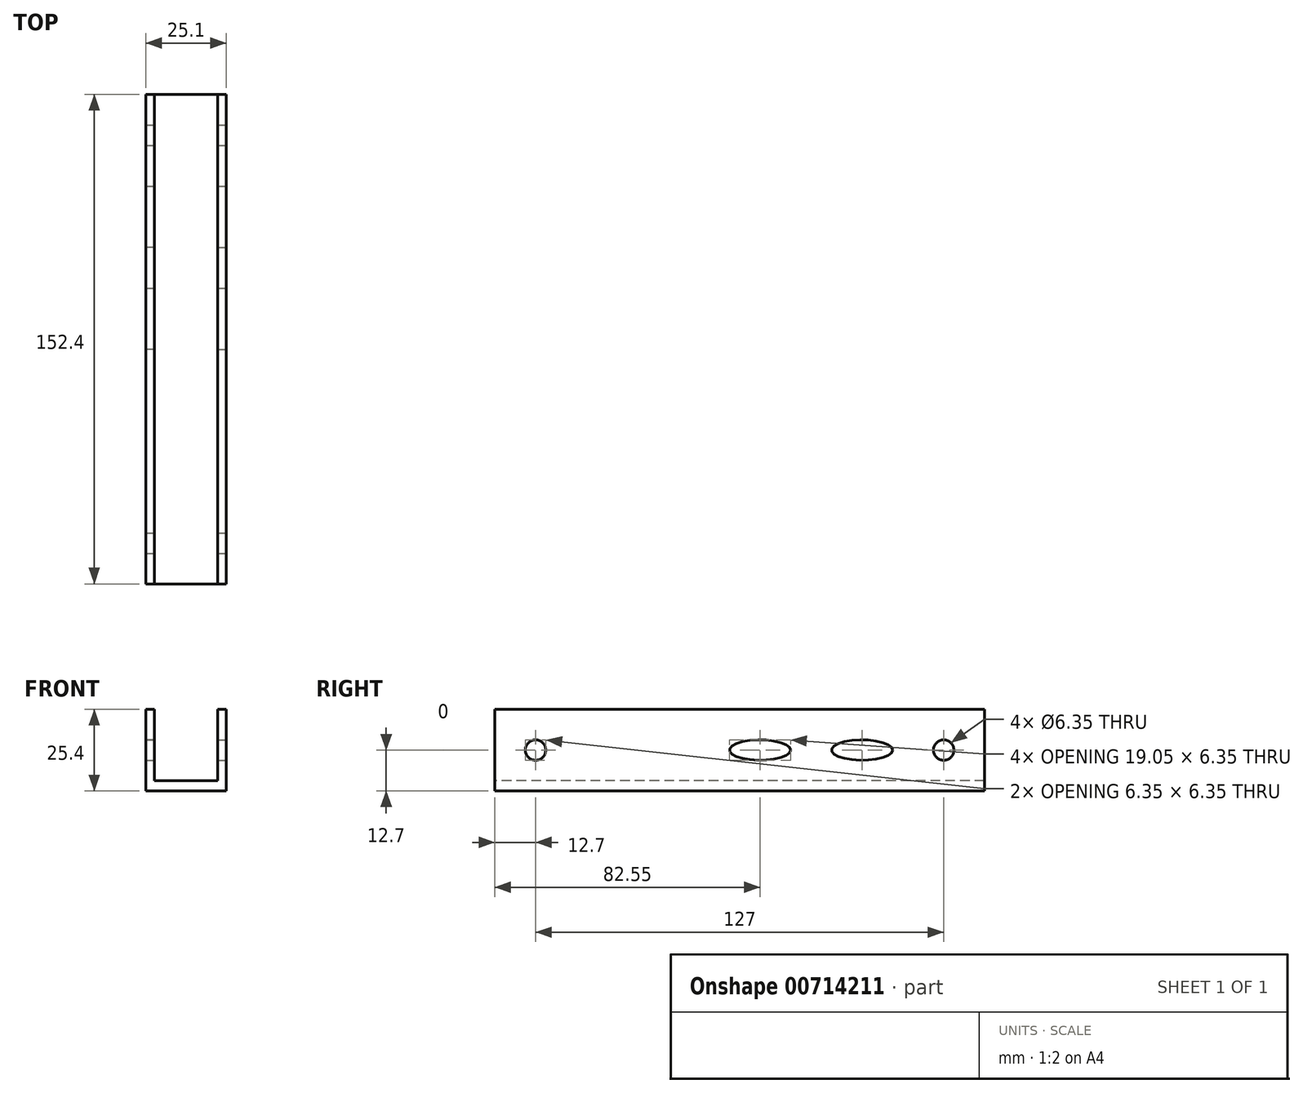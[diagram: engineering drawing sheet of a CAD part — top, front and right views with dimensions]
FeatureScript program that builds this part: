
annotation { "Feature Type Name" : "Feature", "Feature Type Description" : "" }
export const myFeature = defineFeature(function(context is Context, id is Id, definition is map)
    precondition{}
    {
        {
            var Q0;
            Q0=qCreatedBy(makeId("Front.planeOp"),FACE);
            var sketch = newSketch(context, id + "F0", { "sketchPlane" : qUnion([Q0])});
            skLineSegment(sketch, "E0.bottom", {"start": v(12.55, 12.7) * mm, "end": v(-12.55, 12.7) * mm});
            skLineSegment(sketch, "E0.top", {"start": v(12.55, -12.7) * mm, "end": v(-12.55, -12.7) * mm});
            skLineSegment(sketch, "E0.left", {"start": v(12.55, 12.7) * mm, "end": v(12.55, -12.7) * mm});
            skLineSegment(sketch, "E0.right", {"start": v(-12.55, 12.7) * mm, "end": v(-12.55, -12.7) * mm});
            skPoint(sketch, "E0.middle", {"position": v(0, 0) * mm});
            skSolve(sketch);
        }
        {
            var Q0;
            Q0 = qSketchRegion(id + "F0", true);
            extrude(context, id + "F1", {"entities" : qUnion([Q0]), "depth" : 152.4 * mm, "offsetDistance" : 25.4 * mm});
        }
        {
            var Q0;
            Q0=makeQuery(id+"F1.opExtrude","CAP_FACE",FACE,{"disambiguationData":[OSD([sQuery(id+"F0.wireOp",EDGE,"E0.bottom"),sQuery(id+"F0.wireOp",EDGE,"E0.top"),sQuery(id+"F0.wireOp",EDGE,"E0.left"),sQuery(id+"F0.wireOp",EDGE,"E0.right")])],"isStart":false});
            var sketch = newSketch(context, id + "F2", { "sketchPlane" : qUnion([Q0])});
            skLineSegment(sketch, "E1.bottom", {"start": v(9.85, 9.52) * mm, "end": v(-9.85, 9.52) * mm});
            skLineSegment(sketch, "E1.top", {"start": v(9.85, -9.52) * mm, "end": v(-9.85, -9.52) * mm});
            skLineSegment(sketch, "E1.left", {"start": v(9.85, 9.52) * mm, "end": v(9.85, -9.52) * mm});
            skLineSegment(sketch, "E1.right", {"start": v(-9.85, 9.52) * mm, "end": v(-9.85, -9.52) * mm});
            skPoint(sketch, "E1.middle", {"position": v(0, 0) * mm});
            skSolve(sketch);
        }
        {
            var Q0;
            Q0 = qSketchRegion(id + "F2", true);
            extrude(context, id + "F3", {"entities" : qUnion([Q0]), "operationType" : NewBodyOperationType.REMOVE, "oppositeDirection" : true, "depth" : 203.2 * mm, "offsetDistance" : 25.4 * mm});
        }
        {
            var Q0;
            Q0=makeQuery(id+"F1.opExtrude","SWEPT_FACE",FACE,{"disambiguationData":[OSD([sQuery(id+"F0.wireOp",EDGE,"E0.left")])]});
            var sketch = newSketch(context, id + "F4", { "sketchPlane" : qUnion([Q0])});
            skCircle(sketch, "E2", {"center": v(-139.7, 0) * mm, "radius": 3.18 * mm});
            skSolve(sketch);
        }
        {
            var Q0;
            Q0=makeQuery(id+"F4.imprint","IMPRINT",FACE,{"disambiguationData":[TD([[makeQuery(id+"F4.imprint","IMPRINT",EDGE,{"derivedFrom":sQuery(id+"F4.wireOp",EDGE,"E2")}),1.0]])]});
            extrude(context, id + "F5", {"entities" : qUnion([Q0]), "operationType" : NewBodyOperationType.REMOVE, "oppositeDirection" : true, "depth" : 25.4 * mm, "offsetDistance" : 25.4 * mm});
        }
        {
            var Q0;
            Q0=makeQuery(id+"F1.opExtrude","CAP_FACE",FACE,{"disambiguationData":[OSD([sQuery(id+"F0.wireOp",EDGE,"E0.bottom"),sQuery(id+"F0.wireOp",EDGE,"E0.top"),sQuery(id+"F0.wireOp",EDGE,"E0.left"),sQuery(id+"F0.wireOp",EDGE,"E0.right")])],"isStart":true});
            var sketch = newSketch(context, id + "F6", { "sketchPlane" : qUnion([Q0])});
            skLineSegment(sketch, "E3.bottom", {"start": v(-9.85, 9.52) * mm, "end": v(9.85, 9.52) * mm});
            skLineSegment(sketch, "E3.top", {"start": v(-9.85, 12.7) * mm, "end": v(9.85, 12.7) * mm});
            skLineSegment(sketch, "E3.left", {"start": v(-9.85, 9.52) * mm, "end": v(-9.85, 12.7) * mm});
            skLineSegment(sketch, "E3.right", {"start": v(9.85, 9.52) * mm, "end": v(9.85, 12.7) * mm});
            skSolve(sketch);
        }
        {
            var Q0;
            Q0 = qSketchRegion(id + "F6", true);
            extrude(context, id + "F7", {"entities" : qUnion([Q0]), "operationType" : NewBodyOperationType.REMOVE, "oppositeDirection" : true, "depth" : 203.2 * mm, "offsetDistance" : 25.4 * mm});
        }
        {
            var Q0;
            Q0=makeQuery(id+"F1.opExtrude","SWEPT_FACE",FACE,{"disambiguationData":[OSD([sQuery(id+"F0.wireOp",EDGE,"E0.left")])]});
            var sketch = newSketch(context, id + "F8", { "sketchPlane" : qUnion([Q0])});
            skCircle(sketch, "E4", {"center": v(-12.7, 0) * mm, "radius": 3.18 * mm});
            skEllipse(sketch, "E5", {"center": v(-69.85, 0) * mm, "majorRadius": 9.53 * mm, "minorRadius": 3.18 * mm, "majorAxis": v(1, 0)});
            skEllipse(sketch, "E6", {"center": v(-38.1, 0) * mm, "majorRadius": 9.53 * mm, "minorRadius": 3.18 * mm, "majorAxis": v(1, 0)});
            skSolve(sketch);
        }
        {
            var Q0;
            Q0 = qSketchRegion(id + "F8", true);
            extrude(context, id + "F9", {"entities" : qUnion([Q0]), "operationType" : NewBodyOperationType.REMOVE, "endBound" : BoundingType.THROUGH_ALL, "oppositeDirection" : true, "depth" : 25.4 * mm, "offsetDistance" : 25.4 * mm});
        }
    });
